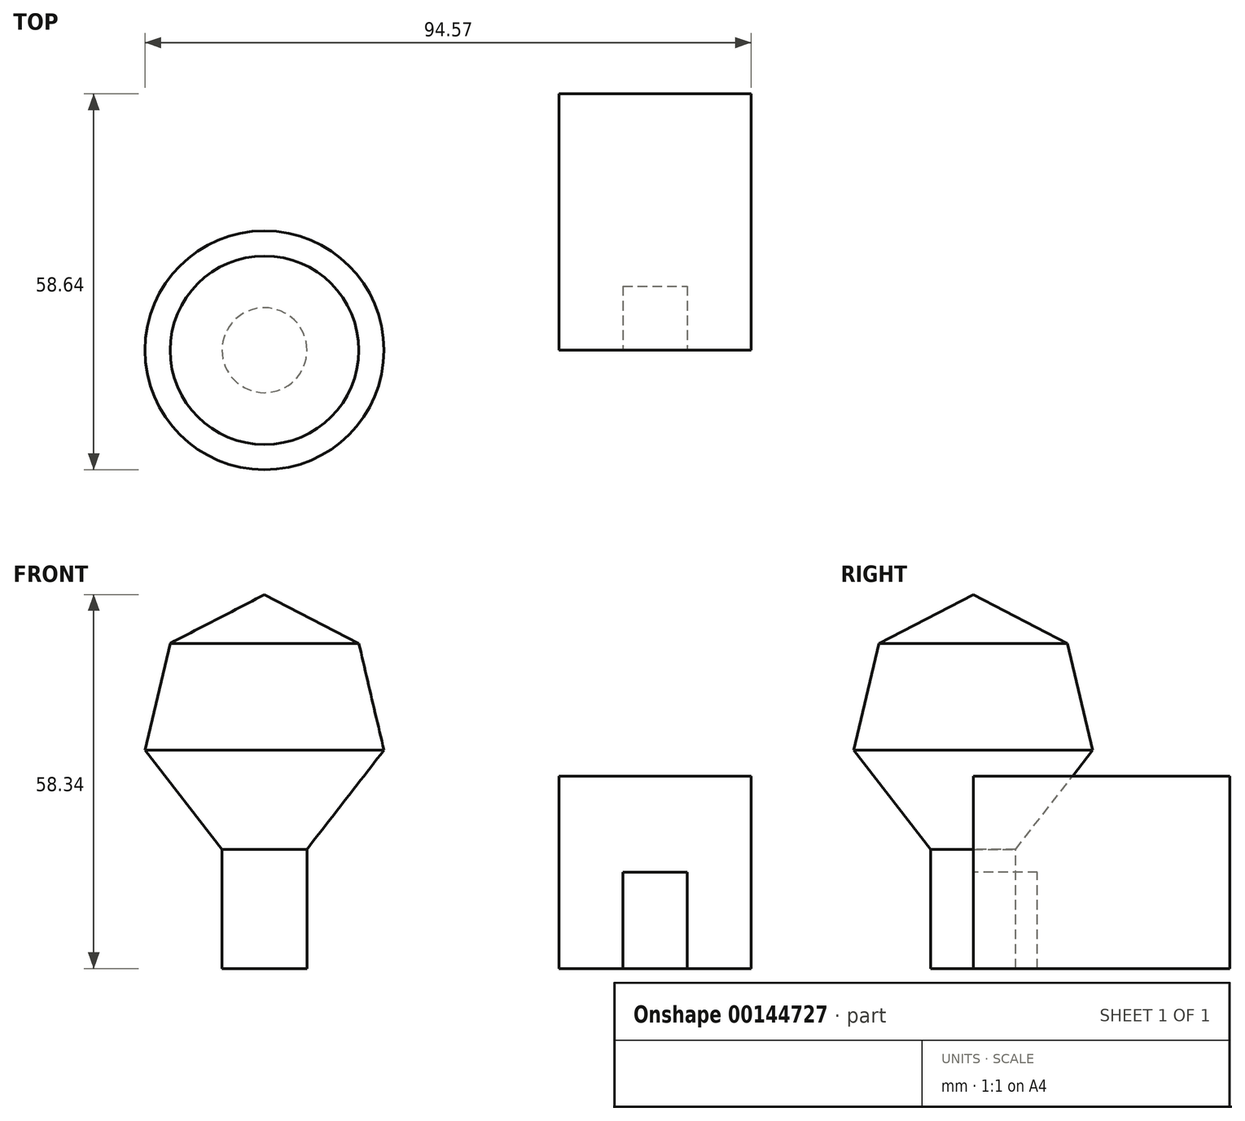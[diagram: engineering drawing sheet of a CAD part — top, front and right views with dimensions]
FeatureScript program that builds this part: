
annotation { "Feature Type Name" : "Feature", "Feature Type Description" : "" }
export const myFeature = defineFeature(function(context is Context, id is Id, definition is map)
    precondition{}
    {
        {
            var Q0;
            Q0=qCreatedBy(makeId("Top.planeOp"),FACE);
            var sketch = newSketch(context, id + "F0", { "sketchPlane" : qUnion([Q0])});
            skLineSegment(sketch, "E0.bottom", {"start": v(0, 0) * mm, "end": v(30, 0) * mm});
            skLineSegment(sketch, "E0.top", {"start": v(0, 40) * mm, "end": v(30, 40) * mm});
            skLineSegment(sketch, "E0.left", {"start": v(0, 0) * mm, "end": v(0, 40) * mm});
            skLineSegment(sketch, "E0.right", {"start": v(30, 0) * mm, "end": v(30, 40) * mm});
            skSolve(sketch);
        }
        {
            var Q0;
            Q0=makeQuery(id+"F0.imprint","IMPRINT",FACE,{"disambiguationData":[TD([[makeQuery(id+"F0.imprint","IMPRINT",EDGE,{"derivedFrom":sQuery(id+"F0.wireOp",EDGE,"E0.bottom")}),1.0]])]});
            extrude(context, id + "F1", {"entities" : qUnion([Q0]), "depth" : 30 * mm});
        }
        {
            var Q0;
            Q0=makeQuery(id+"F1.opExtrude","SWEPT_FACE",FACE,{"disambiguationData":[OSD([sQuery(id+"F0.wireOp",EDGE,"E0.bottom")])]});
            var sketch = newSketch(context, id + "F2", { "sketchPlane" : qUnion([Q0])});
            skLineSegment(sketch, "E1.bottom", {"start": v(10, 0) * mm, "end": v(20, 0) * mm});
            skLineSegment(sketch, "E1.top", {"start": v(10, 15) * mm, "end": v(20, 15) * mm});
            skLineSegment(sketch, "E1.left", {"start": v(10, 0) * mm, "end": v(10, 15) * mm});
            skLineSegment(sketch, "E1.right", {"start": v(20, 0) * mm, "end": v(20, 15) * mm});
            skSolve(sketch);
        }
        {
            var Q0;
            Q0=makeQuery(id+"F2.imprint","IMPRINT",FACE,{"disambiguationData":[TD([[makeQuery(id+"F2.imprint","IMPRINT",EDGE,{"derivedFrom":sQuery(id+"F2.wireOp",EDGE,"E1.bottom")}),1.0]])]});
            extrude(context, id + "F3", {"entities" : qUnion([Q0]), "operationType" : NewBodyOperationType.REMOVE, "oppositeDirection" : true, "depth" : 10 * mm});
        }
        {
            var Q0;
            Q0=qCreatedBy(makeId("Front.planeOp"),FACE);
            var sketch = newSketch(context, id + "F4", { "sketchPlane" : qUnion([Q0])});
            skLineSegment(sketch, "E2", {"start": v(-52.55, 18.6) * mm, "end": v(-64.57, 34.06) * mm});
            skLineSegment(sketch, "E3", {"start": v(-64.57, 34.06) * mm, "end": v(-60.64, 50.73) * mm});
            skLineSegment(sketch, "E4", {"start": v(-60.64, 50.73) * mm, "end": v(-45.93, 58.34) * mm});
            skLineSegment(sketch, "E5", {"start": v(-45.93, 58.34) * mm, "end": v(-45.93, 0) * mm});
            skLineSegment(sketch, "E6", {"start": v(-45.93, 0) * mm, "end": v(-52.55, 0) * mm});
            skLineSegment(sketch, "E7", {"start": v(-52.55, 0) * mm, "end": v(-52.55, 18.6) * mm});
            skSolve(sketch);
        }
        {
            var Q0;
            Q0 = qSketchRegion(id + "F4", true);
            var Q1;
            Q1=sQuery(id+"F4.wireOp",EDGE,"E5");
            revolve(context, id + "F5", {"entities" : qUnion([Q0]), "axis" : qUnion([Q1]), "revolveType" : RevolveType.FULL});
        }
    });
